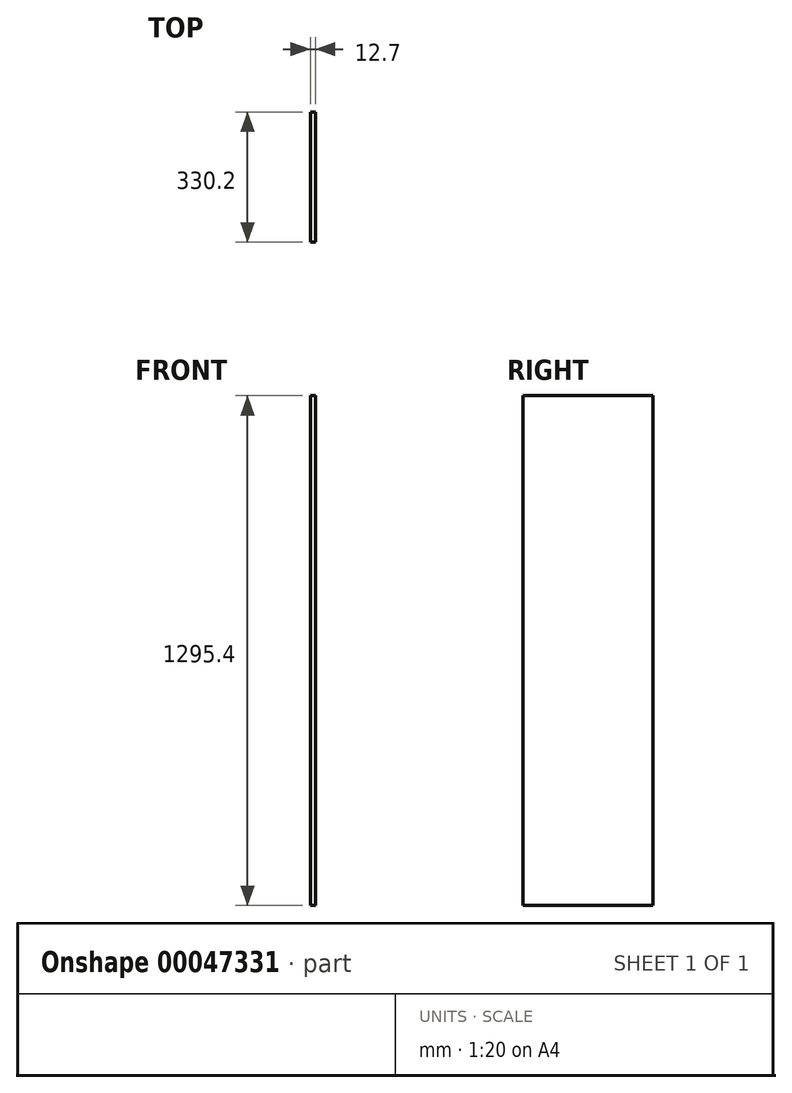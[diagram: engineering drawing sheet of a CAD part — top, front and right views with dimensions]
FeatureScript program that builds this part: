
annotation { "Feature Type Name" : "Feature", "Feature Type Description" : "" }
export const myFeature = defineFeature(function(context is Context, id is Id, definition is map)
    precondition{}
    {
        {
            var Q0;
            Q0=qCreatedBy(makeId("Right.planeOp"),FACE);
            var sketch = newSketch(context, id + "F0", { "sketchPlane" : qUnion([Q0])});
            skLineSegment(sketch, "E0.bottom", {"start": v(-25.48, 1231.18) * mm, "end": v(304.72, 1231.18) * mm});
            skLineSegment(sketch, "E0.top", {"start": v(-25.48, -64.22) * mm, "end": v(304.72, -64.22) * mm});
            skLineSegment(sketch, "E0.left", {"start": v(-25.48, 1231.18) * mm, "end": v(-25.48, -64.22) * mm});
            skLineSegment(sketch, "E0.right", {"start": v(304.72, 1231.18) * mm, "end": v(304.72, -64.22) * mm});
            skSolve(sketch);
        }
        {
            var Q0;
            Q0=makeQuery(id+"F0.imprint","IMPRINT",FACE,{"disambiguationData":[TD([[makeQuery(id+"F0.imprint","IMPRINT",EDGE,{"derivedFrom":sQuery(id+"F0.wireOp",EDGE,"E0.bottom")}),-1.0]])]});
            extrude(context, id + "F1", {"entities" : qUnion([Q0]), "depth" : 12.7 * mm});
        }
    });
